# Revit family: equip-water-cooler-hlsy-tylr-hvr-hd-bi-level
name_source: partatom
category: Plumbing Fixtures
units: mm (PartAtom-declared; Revit-internal decimal feet)

## family parameters
Always vertical = Yes
Cut with Voids When Loaded = No
OmniClass Number = 23.45.00.00
OmniClass Title = Sanitary, Laundry, and Cleaning Equipment
Part Type = Normal
Room Calculation Point = No
Round Connector Dimension = Use Radius
Shared = No
Work Plane-Based = No

## types (1)
- equip-water-cooler-hlsy-tylr-hvr-hd-bi-level
    Activation = VR Pushbutton
    Apparent Load Phase 1 = 0 VA
    Basin Material = Metal - Steel - Stainless - Chrome
    Bubbler = VR Bubbler
    CW Connection = Yes
    Cooler Depth = 1' - 6 9/16"
    Cooler Height = 1' - 8 7/16"
    Cooler Width = 3' - 0 1/2"
    Description = ADA Vandal Resistant Cooler
    Dispenser Height = 2' - 3"
    Filter = **ACC (HWF172)
    HW Connection = No
    Left = 7256000083 (Upper)
    Louver Screens = -
    Manufacturer = Halsey Taylor
    Model = HVR8HD-BL 14GA ADA VR CLR
    Number of Poles = 1
    Orifice Height = 2' - 8 9/16"
    Other Features = All include VR pinned torx screws
    Panel Material = Metal - Steel - Stainless - Chrome
    Power Factor = 0
    Refrigerated = Yes
    Right = 8256080083 (Lower)
    Rim Height = 2' - 7 1/2"
    Sanitary Connector Description = Sanitary Connection
    Sanitary Service Size Radius = 0' - 0 5/8"
    Specification = http://www.halseytaylor.com
    Type = Bi-Level
    URL = http://www.halseytaylor.com
    Vent Connection = No
    Version = 1.0.0.0
    Volts/Hertz = 115V/60Hz
    Waste Connection = Yes
    Water Connector Description = Water Supply
    Water Service Flow = 0 GPM
    Water Service Size Radius = 0' - 0 1/4"

## geometry (parser evidence)
native form markers: Sweep x4
no freeform markers — native parametric forms only
